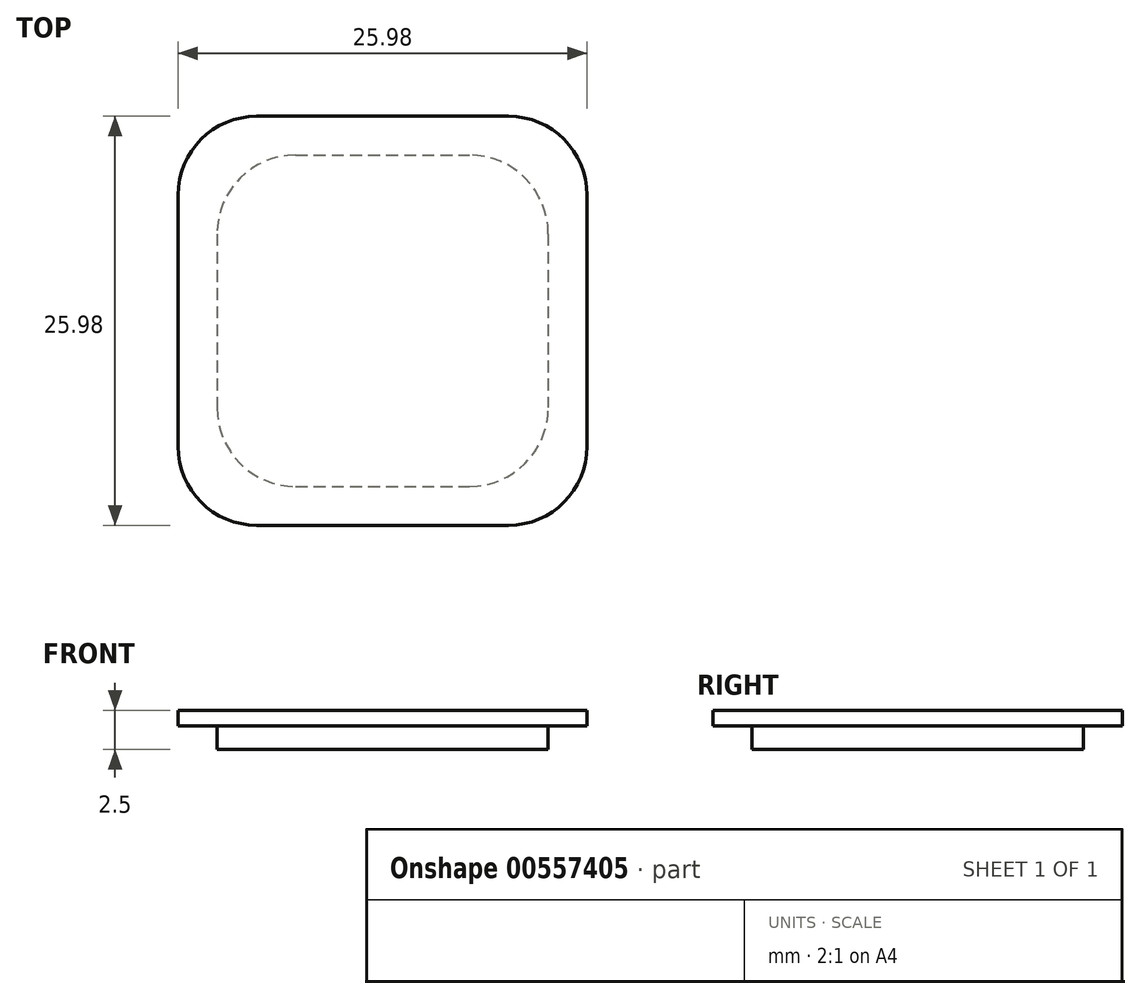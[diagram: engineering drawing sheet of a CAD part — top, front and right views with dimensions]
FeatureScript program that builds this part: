
annotation { "Feature Type Name" : "Feature", "Feature Type Description" : "" }
export const myFeature = defineFeature(function(context is Context, id is Id, definition is map)
    precondition{}
    {
        {
            var Q0;
            Q0=qCreatedBy(makeId("Top.planeOp"),FACE);
            var sketch = newSketch(context, id + "F0", { "sketchPlane" : qUnion([Q0])});
            skLineSegment(sketch, "E0.bottom", {"start": v(-15, 15) * mm, "end": v(15, 15) * mm, "construction": true});
            skLineSegment(sketch, "E0.top", {"start": v(-15, -15) * mm, "end": v(15, -15) * mm, "construction": true});
            skLineSegment(sketch, "E0.left", {"start": v(-15, 15) * mm, "end": v(-15, -15) * mm, "construction": true});
            skLineSegment(sketch, "E0.right", {"start": v(15, 15) * mm, "end": v(15, -15) * mm, "construction": true});
            skLineSegment(sketch, "E1.0", {"start": v(-13, 13) * mm, "end": v(13, 13) * mm});
            skLineSegment(sketch, "E1.1", {"start": v(-13, 13) * mm, "end": v(-13, -13) * mm});
            skLineSegment(sketch, "E1.2", {"start": v(-13, -13) * mm, "end": v(13, -13) * mm});
            skLineSegment(sketch, "E1.3", {"start": v(13, 13) * mm, "end": v(13, -13) * mm});
            skSolve(sketch);
        }
        {
            var Q0;
            Q0 = qSketchRegion(id + "F0", true);
            extrude(context, id + "F1", {"entities" : qUnion([Q0]), "depth" : 1 * mm, "offsetDistance" : 25 * mm});
        }
        {
            var Q0;
            Q0=makeQuery(id+"F1.opExtrude","SWEPT_EDGE",EDGE,{"disambiguationData":[OSD([sQuery(id+"F0.wireOp",EDGE,"E1.1"),sQuery(id+"F0.wireOp",EDGE,"E1.2")])]});
            var Q1;
            Q1=makeQuery(id+"F1.opExtrude","SWEPT_EDGE",EDGE,{"disambiguationData":[OSD([sQuery(id+"F0.wireOp",EDGE,"E1.2"),sQuery(id+"F0.wireOp",EDGE,"E1.3")])]});
            var Q2;
            Q2=makeQuery(id+"F1.opExtrude","SWEPT_EDGE",EDGE,{"disambiguationData":[OSD([sQuery(id+"F0.wireOp",EDGE,"E1.0"),sQuery(id+"F0.wireOp",EDGE,"E1.3")])]});
            var Q3;
            Q3=makeQuery(id+"F1.opExtrude","SWEPT_EDGE",EDGE,{"disambiguationData":[OSD([sQuery(id+"F0.wireOp",EDGE,"E1.0"),sQuery(id+"F0.wireOp",EDGE,"E1.1")])]});
            fillet(context, id + "F2", {"entities" : qUnion([Q0, Q1, Q2, Q3]), "radius" : 5 * mm, "tangentPropagation" : true, "allowEdgeOverflow" : false});
        }
        {
            var Q0;
            Q0=makeQuery(id+"F1.opExtrude","CAP_FACE",FACE,{"disambiguationData":[OSD([sQuery(id+"F0.wireOp",EDGE,"E1.0"),sQuery(id+"F0.wireOp",EDGE,"E1.1"),sQuery(id+"F0.wireOp",EDGE,"E1.2"),sQuery(id+"F0.wireOp",EDGE,"E1.3")])],"isStart":true});
            var sketch = newSketch(context, id + "F3", { "sketchPlane" : qUnion([Q0])});
            skLineSegment(sketch, "E2.0", {"start": v(10.52, -10.52) * mm, "end": v(10.52, 10.52) * mm});
            skLineSegment(sketch, "E2.1", {"start": v(-10.52, -10.52) * mm, "end": v(10.52, -10.52) * mm});
            skLineSegment(sketch, "E2.2", {"start": v(-10.52, -10.52) * mm, "end": v(-10.52, 10.52) * mm});
            skLineSegment(sketch, "E2.3", {"start": v(-10.52, 10.52) * mm, "end": v(10.52, 10.52) * mm});
            skSolve(sketch);
        }
        {
            var Q0;
            Q0 = qSketchRegion(id + "F3", true);
            extrude(context, id + "F4", {"entities" : qUnion([Q0]), "operationType" : NewBodyOperationType.ADD, "depth" : 1.5 * mm, "offsetDistance" : 25 * mm});
        }
        {
            var Q0;
            Q0=makeQuery(id+"F4.opExtrude","SWEPT_EDGE",EDGE,{"disambiguationData":[OSD([sQuery(id+"F3.wireOp",EDGE,"E2.0"),sQuery(id+"F3.wireOp",EDGE,"E2.3")])]});
            var Q1;
            Q1=makeQuery(id+"F4.opExtrude","SWEPT_EDGE",EDGE,{"disambiguationData":[OSD([sQuery(id+"F3.wireOp",EDGE,"E2.2"),sQuery(id+"F3.wireOp",EDGE,"E2.3")])]});
            var Q2;
            Q2=makeQuery(id+"F4.opExtrude","SWEPT_EDGE",EDGE,{"disambiguationData":[OSD([sQuery(id+"F3.wireOp",EDGE,"E2.0"),sQuery(id+"F3.wireOp",EDGE,"E2.1")])]});
            var Q3;
            Q3=makeQuery(id+"F4.opExtrude","SWEPT_EDGE",EDGE,{"disambiguationData":[OSD([sQuery(id+"F3.wireOp",EDGE,"E2.1"),sQuery(id+"F3.wireOp",EDGE,"E2.2")])]});
            fillet(context, id + "F5", {"entities" : qUnion([Q0, Q1, Q2, Q3]), "radius" : 5 * mm, "tangentPropagation" : true, "allowEdgeOverflow" : false});
        }
    });
